# Revit family: 1Electronics_Commercial-Audio_Biamp_Preamplifier_Zone-4
name_source: partatom
category: Communication Devices
units: mm (PartAtom-declared; Revit-internal decimal feet)

## family parameters
Cut with Voids When Loaded = No
Host = Face
Maintain Annotation Orientation = No
OmniClass Number = 23.85.10.11.14
OmniClass Title = Audio Equipment
Part Type = Normal
Room Calculation Point = No
Round Connector Dimension = Use Diameter
Shared = No

## types (1)
- ZONE4
    Apparent Load = 25 VA
    Applicable low impedance = Yes
    Connector Description = 90-260 VAC 50/60 Hz
    Crosstalk (dB) = >75
    Default Elevation = 4' - 0"
    Depth = 0' - 7 1/2"
    Description = ZONE4 4-Zone Stereo Pre-Amplifier
    Emergency input = Yes
    Frequency response (in Hz) = 20 - 30 k
    Height = 0' - 1 1/2"
    Housing Material = Biamp - Metal - Black
    Inputs with Phantom power = 2
    Line input balanced = 0
    Line input unbalanced = 4 stereo
    MIC inputs balanced = 3
    MIC inputs unbalanced = 0
    MIC level control = Yes
    Manufacturer = Biamp
    Max Power Consumption = 25 W
    Maximum qty paging Mics = 4
    Model = ZONE4
    Music level control = Yes
    Number of Poles = 1
    Output level balanced (dB) = 0
    Output level unbalanced (dB) = 0
    Power Factor = 1
    Priority levels = 2
    Product Documentation Link = https://downloads.biamp.com
    Product Page URL = https://www.biamp.com
    Product data url = https://www.bimobject.com
    RS232 (serial communication port) = Yes
    Signal to noise level SNR (dB) = >90
    Source selection per zone = Yes
    Tone control = Yes
    Total harmonic distortion TBH (%) = <0.02
    URL = https://www.biamp.com
    Voltage = 120 V
    Wall panel controls = Yes
    Weight = 6.05 lbf
    Width = 1' - 7"
    Zone outputs = 4 Stereo

## geometry (parser evidence)
native form markers: Sweep x2
no freeform markers — native parametric forms only
